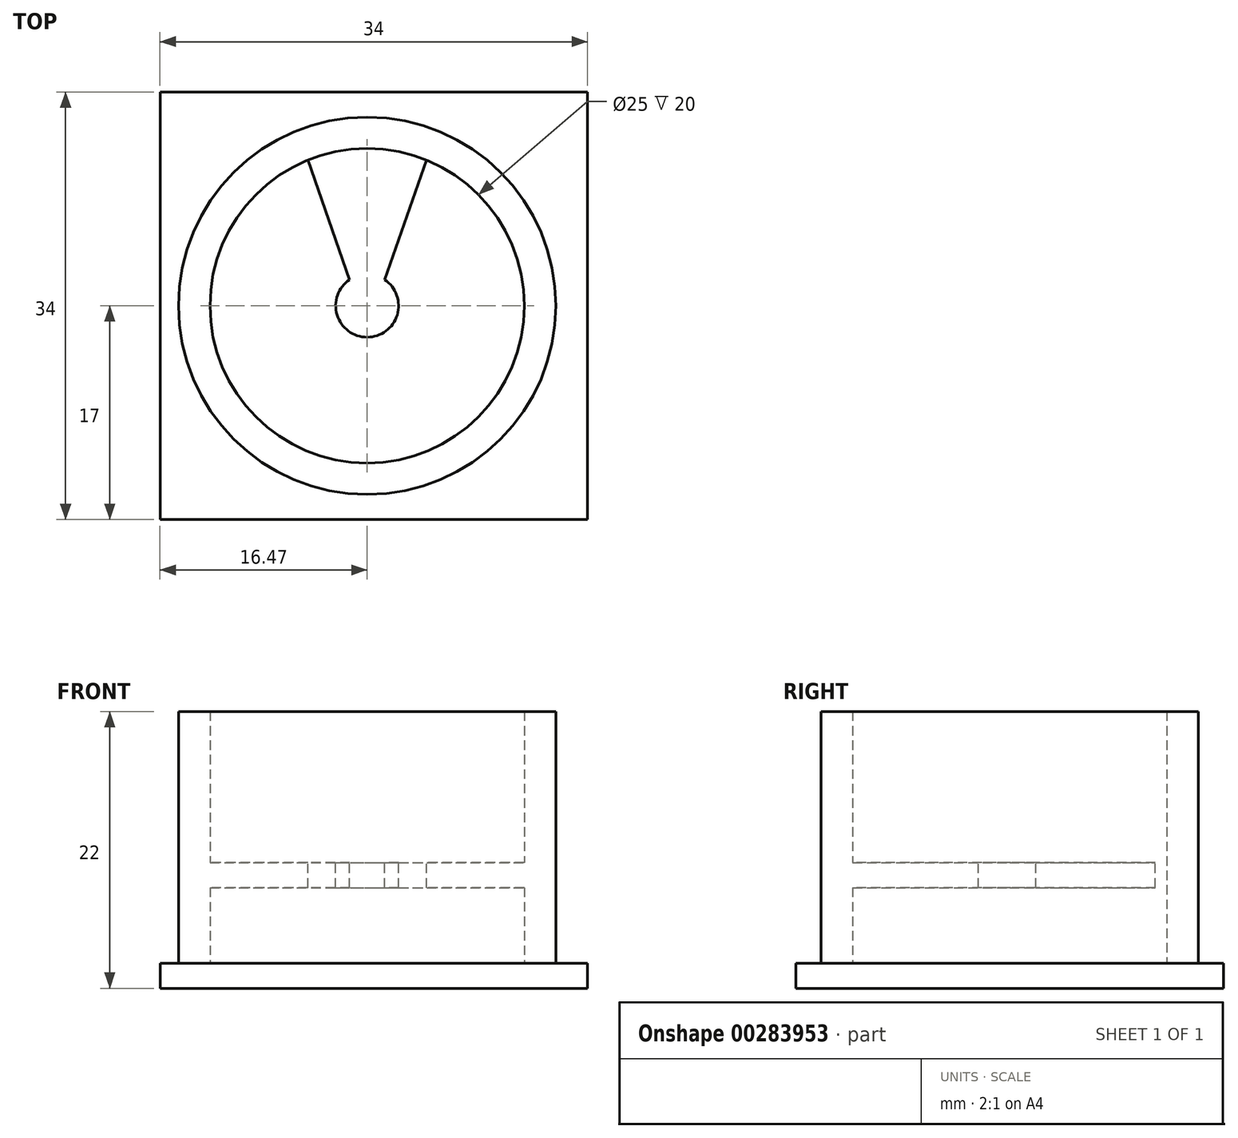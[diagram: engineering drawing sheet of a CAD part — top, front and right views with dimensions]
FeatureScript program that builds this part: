
annotation { "Feature Type Name" : "Feature", "Feature Type Description" : "" }
export const myFeature = defineFeature(function(context is Context, id is Id, definition is map)
    precondition{}
    {
        {
            var Q0;
            Q0=qCreatedBy(makeId("Top.planeOp"),FACE);
            var sketch = newSketch(context, id + "F0", { "sketchPlane" : qUnion([Q0])});
            skCircle(sketch, "E0", {"center": v(0, 0) * mm, "radius": 15 * mm});
            skCircle(sketch, "E1", {"center": v(0, 0) * mm, "radius": 12.5 * mm});
            skSolve(sketch);
        }
        {
            var Q0;
            Q0 = qSketchRegion(id + "F0", true);
            extrude(context, id + "F1", {"entities" : qUnion([Q0]), "depth" : 20 * mm});
        }
        {
            var Q0;
            Q0=qCreatedBy(makeId("Top.planeOp"),FACE);
            cPlane(context, id + "F2", {"entities" : qUnion([Q0]), "cplaneType" : CPlaneType.OFFSET, "offset" : 8 * mm, "width" : 150 * mm, "height" : 150 * mm});
        }
        {
            var Q0;
            Q0=qCreatedBy(id+"F2.planeOp",FACE);
            var sketch = newSketch(context, id + "F3", { "sketchPlane" : qUnion([Q0])});
            skArc(sketch, "E2", {"start": v(-1.4, 2.07) * mm, "mid": v(0, -2.5) * mm, "end": v(1.4, 2.07) * mm});
            skLineSegment(sketch, "E3", {"start": v(-1.4, 2.07) * mm, "end": v(-4.71, 11.58) * mm});
            skLineSegment(sketch, "E4", {"start": v(0, 0) * mm, "end": v(0, 17.22) * mm, "construction": true});
            skLineSegment(sketch, "E5.MirrorCS", {"start": v(1.4, 2.07) * mm, "end": v(4.71, 11.58) * mm});
            skArc(sketch, "E6", {"start": v(-4.71, 11.58) * mm, "mid": v(0, -12.5) * mm, "end": v(4.71, 11.58) * mm});
            skSolve(sketch);
        }
        {
            var Q0;
            Q0 = qSketchRegion(id + "F3", true);
            extrude(context, id + "F4", {"entities" : qUnion([Q0]), "operationType" : NewBodyOperationType.ADD, "oppositeDirection" : true, "depth" : 2 * mm});
        }
        {
            var Q0;
            Q0=qCreatedBy(makeId("Top.planeOp"),FACE);
            var sketch = newSketch(context, id + "F5", { "sketchPlane" : qUnion([Q0])});
            skLineSegment(sketch, "E7.bottom", {"start": v(17.53, -17) * mm, "end": v(-16.47, -17) * mm});
            skLineSegment(sketch, "E7.top", {"start": v(17.53, 17) * mm, "end": v(-16.47, 17) * mm});
            skLineSegment(sketch, "E7.left", {"start": v(17.53, -17) * mm, "end": v(17.53, 17) * mm});
            skLineSegment(sketch, "E7.right", {"start": v(-16.47, -17) * mm, "end": v(-16.47, 17) * mm});
            skSolve(sketch);
        }
        {
            var Q0;
            Q0 = qSketchRegion(id + "F5", true);
            extrude(context, id + "F6", {"entities" : qUnion([Q0]), "operationType" : NewBodyOperationType.ADD, "oppositeDirection" : true, "depth" : 2 * mm});
        }
    });
